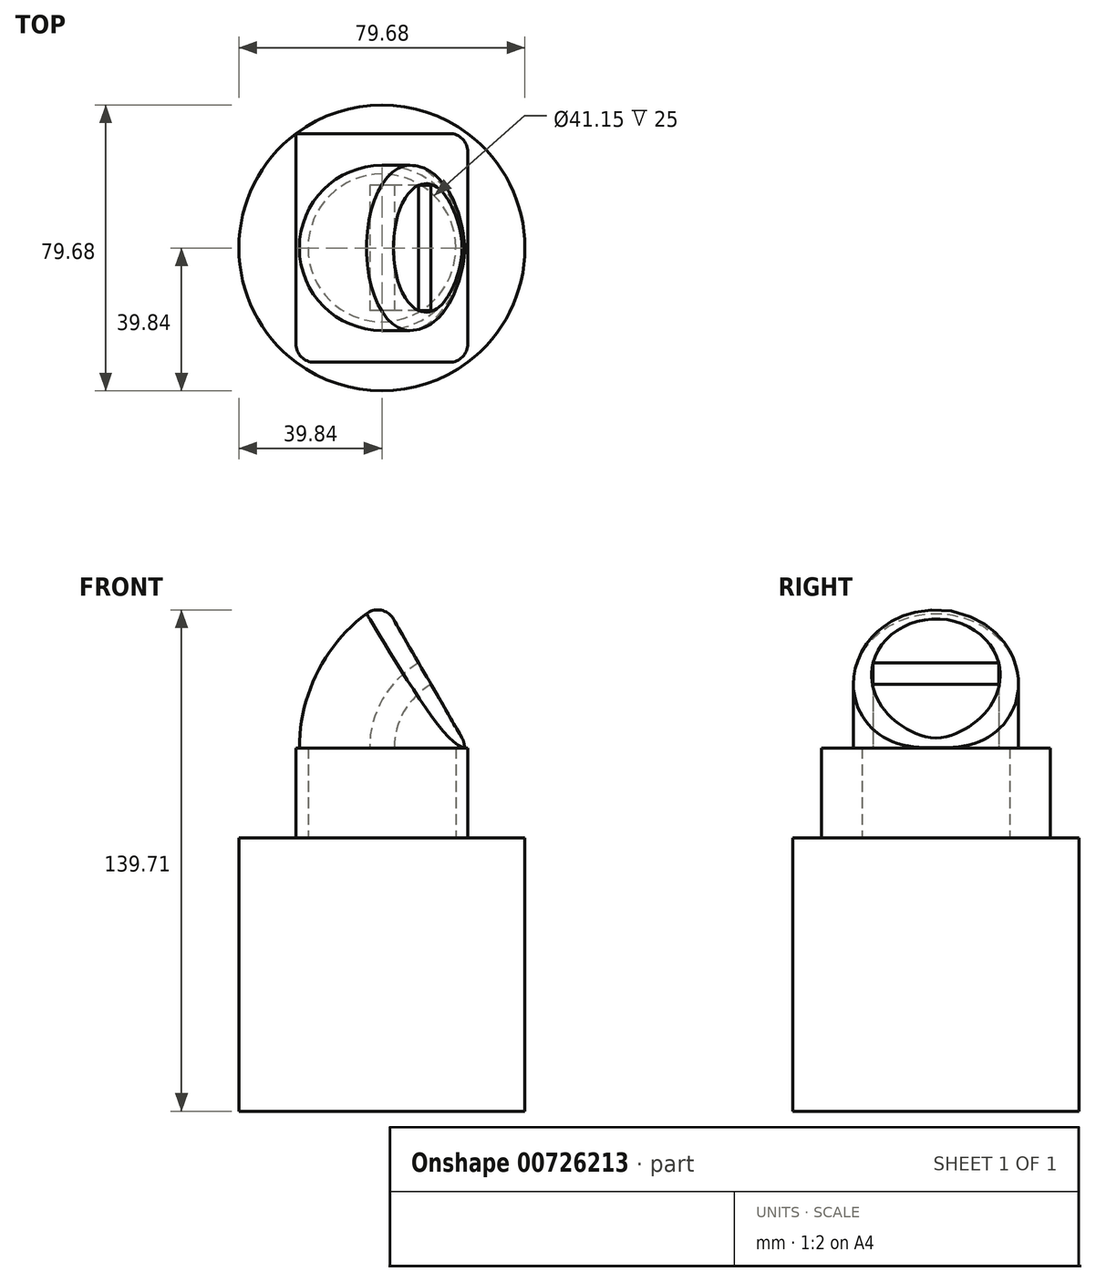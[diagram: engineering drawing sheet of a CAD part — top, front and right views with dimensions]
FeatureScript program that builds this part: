
annotation { "Feature Type Name" : "Feature", "Feature Type Description" : "" }
export const myFeature = defineFeature(function(context is Context, id is Id, definition is map)
    precondition{}
    {
        {
            var Q0;
            Q0=qCreatedBy(makeId("Top.planeOp"),FACE);
            var sketch = newSketch(context, id + "F0", { "sketchPlane" : qUnion([Q0])});
            skCircle(sketch, "E0", {"center": v(0, 0) * mm, "radius": 39.84 * mm});
            skSolve(sketch);
        }
        {
            var Q0;
            Q0 = qSketchRegion(id + "F0", true);
            extrude(context, id + "F1", {"entities" : qUnion([Q0]), "depth" : 76.2 * mm, "offsetDistance" : 25.4 * mm});
        }
        {
            var Q0;
            Q0=makeQuery(id+"F1.opExtrude","CAP_FACE",FACE,{"disambiguationData":[OSD([sQuery(id+"F0.wireOp",EDGE,"E0")])],"isStart":false});
            var sketch = newSketch(context, id + "F2", { "sketchPlane" : qUnion([Q0])});
            skLineSegment(sketch, "E1.bottom", {"start": v(23.92, 31.86) * mm, "end": v(-23.92, 31.86) * mm});
            skLineSegment(sketch, "E1.top", {"start": v(23.92, -31.86) * mm, "end": v(-23.92, -31.86) * mm});
            skLineSegment(sketch, "E1.left", {"start": v(23.92, 31.86) * mm, "end": v(23.92, -31.86) * mm});
            skLineSegment(sketch, "E1.right", {"start": v(-23.92, 31.86) * mm, "end": v(-23.92, -31.86) * mm});
            skPoint(sketch, "E1.middle", {"position": v(0, 0) * mm});
            skCircle(sketch, "E2", {"center": v(0, 0) * mm, "radius": 20.58 * mm});
            skSolve(sketch);
        }
        {
            var Q0;
            Q0 = qSketchRegion(id + "F2", true);
            extrude(context, id + "F3", {"entities" : qUnion([Q0]), "operationType" : NewBodyOperationType.ADD, "depth" : 25 * mm, "offsetDistance" : 25.4 * mm});
        }
        {
            var Q0;
            Q0=makeQuery(id+"F3.opExtrude","CAP_FACE",FACE,{"disambiguationData":[OSD([sQuery(id+"F2.wireOp",EDGE,"E1.bottom"),sQuery(id+"F2.wireOp",EDGE,"E1.top"),sQuery(id+"F2.wireOp",EDGE,"E1.left"),sQuery(id+"F2.wireOp",EDGE,"E1.right"),sQuery(id+"F2.wireOp",EDGE,"E2")])],"isStart":false});
            var sketch = newSketch(context, id + "F4", { "sketchPlane" : qUnion([Q0])});
            skCircle(sketch, "E3", {"center": v(0, 0) * mm, "radius": 23 * mm});
            skLineSegment(sketch, "E4.bottom", {"start": v(3.45, 17.51) * mm, "end": v(-3.45, 17.51) * mm});
            skLineSegment(sketch, "E4.top", {"start": v(3.45, -17.51) * mm, "end": v(-3.45, -17.51) * mm});
            skLineSegment(sketch, "E4.left", {"start": v(3.45, 17.51) * mm, "end": v(3.45, -17.51) * mm});
            skLineSegment(sketch, "E4.right", {"start": v(-3.45, 17.51) * mm, "end": v(-3.45, -17.51) * mm});
            skLineSegment(sketch, "E5", {"start": v(23.92, 26.03) * mm, "end": v(23.92, -19.4) * mm});
            skSolve(sketch);
        }
        {
            var Q0;
            Q0 = qSketchRegion(id + "F4", true);
            var Q1;
            Q1=sQuery(id+"F4.wireOp",EDGE,"E5");
            revolve(context, id + "F5", {"operationType" : NewBodyOperationType.ADD, "surfaceOperationType" : NewSurfaceOperationType.NEW, "entities" : qUnion([Q0]), "axis" : qUnion([Q1]), "revolveType" : RevolveType.ONE_DIRECTION, "oppositeDirection" : true, "angle" : 60 * degree});
        }
        {
            var Q0;
            Q0=makeQuery(id+"F5.opRevolve","CAP_EDGE",EDGE,{"disambiguationData":[OSD([sQuery(id+"F4.wireOp",EDGE,"E3")])],"isStart":false});
            fillet(context, id + "F6", {"entities" : qUnion([Q0]), "radius" : 5.08 * mm, "tangentPropagation" : true, "allowEdgeOverflow" : false});
        }
        {
            var Q0;
            Q0=makeQuery(id+"F3.opExtrude","SWEPT_EDGE",EDGE,{"disambiguationData":[OSD([sQuery(id+"F0.wireOp",EDGE,"E0"),sQuery(id+"F2.wireOp",EDGE,"E1.top"),sQuery(id+"F2.wireOp",EDGE,"E1.left")])]});
            var Q1;
            Q1=makeQuery(id+"F3.opExtrude","SWEPT_EDGE",EDGE,{"disambiguationData":[OSD([sQuery(id+"F0.wireOp",EDGE,"E0"),sQuery(id+"F2.wireOp",EDGE,"E1.bottom"),sQuery(id+"F2.wireOp",EDGE,"E1.left")])]});
            var Q2;
            Q2=makeQuery(id+"F3.opExtrude","SWEPT_EDGE",EDGE,{"disambiguationData":[OSD([sQuery(id+"F0.wireOp",EDGE,"E0"),sQuery(id+"F2.wireOp",EDGE,"E1.top"),sQuery(id+"F2.wireOp",EDGE,"E1.right")])]});
            fillet(context, id + "F7", {"entities" : qUnion([Q0, Q1, Q2]), "radius" : 5.08 * mm, "tangentPropagation" : true, "allowEdgeOverflow" : false});
        }
    });
